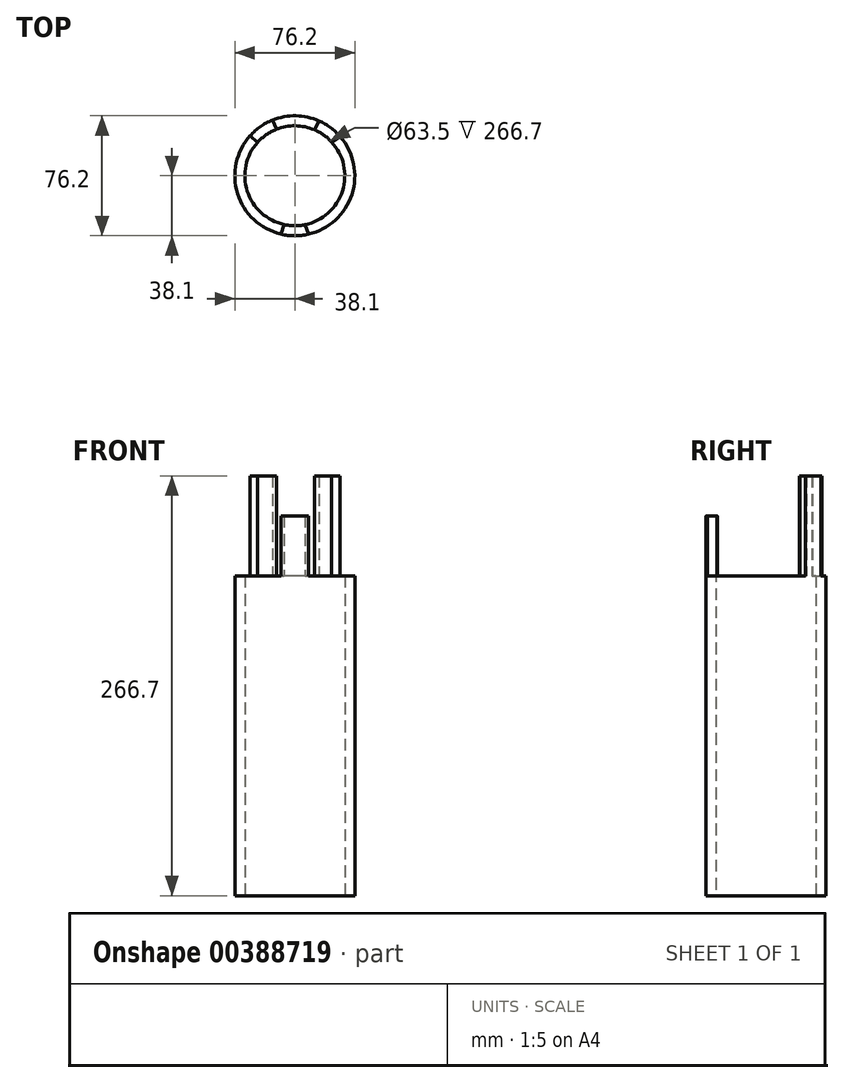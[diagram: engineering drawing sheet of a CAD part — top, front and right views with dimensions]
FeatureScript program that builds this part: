
annotation { "Feature Type Name" : "Feature", "Feature Type Description" : "" }
export const myFeature = defineFeature(function(context is Context, id is Id, definition is map)
    precondition{}
    {
        {
            var Q0;
            Q0=qCreatedBy(makeId("Top.planeOp"),FACE);
            var sketch = newSketch(context, id + "F0", { "sketchPlane" : qUnion([Q0])});
            skCircle(sketch, "E0", {"center": v(0, 0) * mm, "radius": 38.1 * mm});
            skCircle(sketch, "E1", {"center": v(0, 0) * mm, "radius": 31.75 * mm});
            skSolve(sketch);
        }
        {
            var Q0;
            Q0=makeQuery(id+"F0.imprint","IMPRINT",FACE,{"disambiguationData":[TD([[makeQuery(id+"F0.imprint","IMPRINT",EDGE,{"derivedFrom":sQuery(id+"F0.wireOp",EDGE,"E0")}),1.0]])]});
            extrude(context, id + "F1", {"entities" : qUnion([Q0]), "depth" : 203.2 * mm});
        }
        {
            var Q0;
            Q0=makeQuery(id+"F1.opExtrude","CAP_FACE",FACE,{"disambiguationData":[OSD([sQuery(id+"F0.wireOp",EDGE,"E0"),sQuery(id+"F0.wireOp",EDGE,"E1")])],"isStart":false});
            var sketch = newSketch(context, id + "F2", { "sketchPlane" : qUnion([Q0])});
            skLineSegment(sketch, "E2", {"start": v(-6.76, -31.02) * mm, "end": v(-8.82, -37.07) * mm});
            skLineSegment(sketch, "E3", {"start": v(6.46, -31.09) * mm, "end": v(8.57, -37.12) * mm});
            skLineSegment(sketch, "E4", {"start": v(-11.74, 29.5) * mm, "end": v(-14.21, 35.35) * mm});
            skLineSegment(sketch, "E5", {"start": v(-23.62, 21.22) * mm, "end": v(-28.32, 25.5) * mm});
            skLineSegment(sketch, "E6", {"start": v(12.42, 29.22) * mm, "end": v(15.4, 34.85) * mm});
            skLineSegment(sketch, "E7", {"start": v(23.35, 21.52) * mm, "end": v(28.8, 24.94) * mm});
            skSolve(sketch);
        }
        {
            var Q0;
            {var subQ0=sQuery(id+"F2.wireOp",EDGE,"E4");Q0=makeQuery(id+"F2.imprint","IMPRINT",FACE,{"disambiguationData":[TD([[makeQuery(id+"F2.imprint","IMPRINT",EDGE,{"derivedFrom":subQ0}),1.0]])]});}
            var Q1;
            {var subQ0=sQuery(id+"F2.wireOp",EDGE,"E6");Q1=makeQuery(id+"F2.imprint","IMPRINT",FACE,{"disambiguationData":[TD([[makeQuery(id+"F2.imprint","IMPRINT",EDGE,{"derivedFrom":subQ0}),-1.0]])]});}
            extrude(context, id + "F3", {"entities" : qUnion([Q0, Q1]), "operationType" : NewBodyOperationType.ADD, "depth" : 63.5 * mm});
        }
        {
            var Q0;
            {var subQ0=sQuery(id+"F2.wireOp",EDGE,"E2");Q0=makeQuery(id+"F2.imprint","IMPRINT",FACE,{"disambiguationData":[TD([[makeQuery(id+"F2.imprint","IMPRINT",EDGE,{"derivedFrom":subQ0}),1.0]])]});}
            extrude(context, id + "F4", {"entities" : qUnion([Q0]), "operationType" : NewBodyOperationType.ADD, "depth" : 38.1 * mm});
        }
    });
